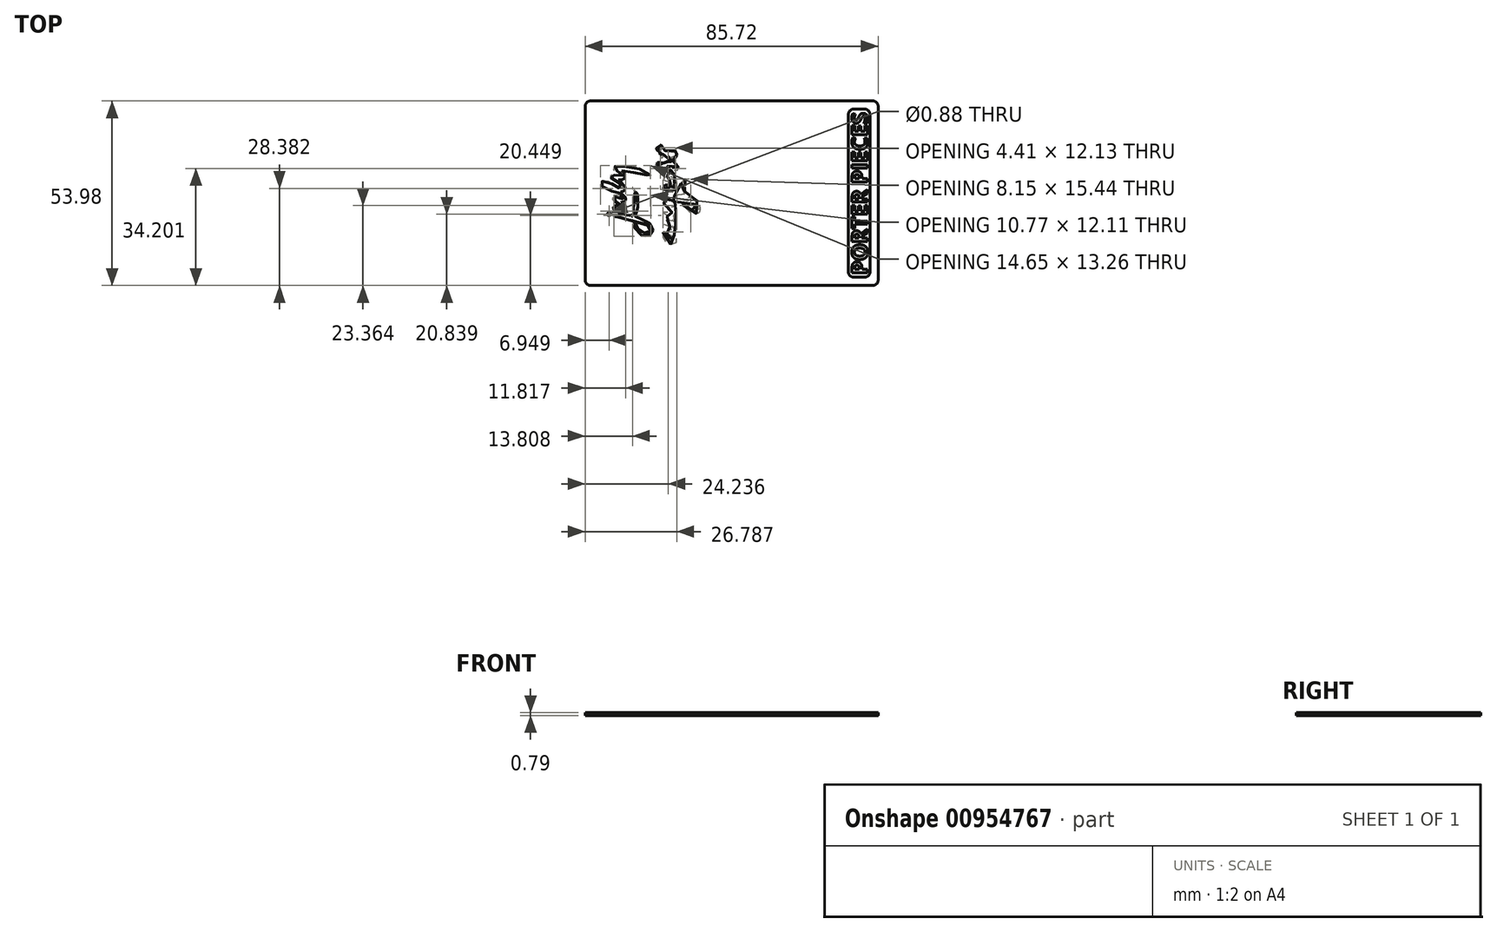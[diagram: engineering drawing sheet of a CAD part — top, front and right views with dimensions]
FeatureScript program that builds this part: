
annotation { "Feature Type Name" : "Feature", "Feature Type Description" : "" }
export const myFeature = defineFeature(function(context is Context, id is Id, definition is map)
    precondition{}
    {
        {
            var Q0;
            Q0=qCreatedBy(makeId("Top.planeOp"),FACE);
            var sketch = newSketch(context, id + "F0", { "sketchPlane" : qUnion([Q0])});
            skLineSegment(sketch, "E0.bottom", {"start": v(42.86, 26.99) * mm, "end": v(-42.86, 26.99) * mm});
            skLineSegment(sketch, "E0.top", {"start": v(42.86, -26.99) * mm, "end": v(-42.86, -26.99) * mm});
            skLineSegment(sketch, "E0.left", {"start": v(42.86, 26.99) * mm, "end": v(42.86, -26.99) * mm});
            skLineSegment(sketch, "E0.right", {"start": v(-42.86, 26.99) * mm, "end": v(-42.86, -26.99) * mm});
            skPoint(sketch, "E0.middle", {"position": v(0, 0) * mm});
            skSolve(sketch);
        }
        {
            var Q0;
            Q0=makeQuery(id+"F0.imprint","IMPRINT",FACE,{"disambiguationData":[TD([[makeQuery(id+"F0.imprint","IMPRINT",EDGE,{"derivedFrom":sQuery(id+"F0.wireOp",EDGE,"E0.bottom")}),1.0]])]});
            extrude(context, id + "F1", {"entities" : qUnion([Q0]), "depth" : 0.8 * mm, "offsetDistance" : 25.4 * mm});
        }
        {
            var Q0;
            Q0=makeQuery(id+"F1.opExtrude","SWEPT_EDGE",EDGE,{"disambiguationData":[OSD([sQuery(id+"F0.wireOp",EDGE,"E0.bottom"),sQuery(id+"F0.wireOp",EDGE,"E0.left")])]});
            var Q1;
            Q1=makeQuery(id+"F1.opExtrude","SWEPT_EDGE",EDGE,{"disambiguationData":[OSD([sQuery(id+"F0.wireOp",EDGE,"E0.bottom"),sQuery(id+"F0.wireOp",EDGE,"E0.right")])]});
            var Q2;
            Q2=makeQuery(id+"F1.opExtrude","SWEPT_EDGE",EDGE,{"disambiguationData":[OSD([sQuery(id+"F0.wireOp",EDGE,"E0.top"),sQuery(id+"F0.wireOp",EDGE,"E0.right")])]});
            var Q3;
            Q3=makeQuery(id+"F1.opExtrude","SWEPT_EDGE",EDGE,{"disambiguationData":[OSD([sQuery(id+"F0.wireOp",EDGE,"E0.top"),sQuery(id+"F0.wireOp",EDGE,"E0.left")])]});
            fillet(context, id + "F2", {"entities" : qUnion([Q0, Q1, Q2, Q3]), "radius" : 1.59 * mm, "tangentPropagation" : true, "allowEdgeOverflow" : false});
        }
        {
            var Q0;
            Q0=makeQuery(id+"F1.opExtrude","CAP_FACE",FACE,{"disambiguationData":[OSD([sQuery(id+"F0.wireOp",EDGE,"E0.bottom"),sQuery(id+"F0.wireOp",EDGE,"E0.top"),sQuery(id+"F0.wireOp",EDGE,"E0.left"),sQuery(id+"F0.wireOp",EDGE,"E0.right")])],"isStart":false});
            var sketch = newSketch(context, id + "F3", { "sketchPlane" : qUnion([Q0])});
            skLineSegment(sketch, "E1.bottom", {"start": v(34.13, -24.6) * mm, "end": v(40.48, -24.6) * mm});
            skLineSegment(sketch, "E1.top", {"start": v(34.13, 24.6) * mm, "end": v(40.48, 24.6) * mm});
            skLineSegment(sketch, "E1.left", {"start": v(34.13, -24.6) * mm, "end": v(34.13, 24.6) * mm});
            skLineSegment(sketch, "E1.right", {"start": v(40.48, -24.6) * mm, "end": v(40.48, 24.6) * mm});
            skSolve(sketch);
        }
        {
            var Q0;
            Q0=makeQuery(id+"F3.imprint","IMPRINT",FACE,{"disambiguationData":[TD([[makeQuery(id+"F3.imprint","IMPRINT",EDGE,{"derivedFrom":sQuery(id+"F3.wireOp",EDGE,"E1.bottom")}),1.0]])]});
            extrude(context, id + "F4", {"entities" : qUnion([Q0]), "operationType" : NewBodyOperationType.REMOVE, "oppositeDirection" : true, "depth" : 0.4 * mm, "offsetDistance" : 25.4 * mm});
        }
        {
            var Q0;
            Q0=makeQuery(id+"F4.boolean.opBoolean","COPY",EDGE,{"derivedFrom":makeQuery(id+"F4.opExtrude","SWEPT_EDGE",EDGE,{"disambiguationData":[OSD([sQuery(id+"F3.wireOp",EDGE,"E1.bottom"),sQuery(id+"F3.wireOp",EDGE,"E1.left")])]})});
            var Q1;
            Q1=makeQuery(id+"F4.boolean.opBoolean","COPY",EDGE,{"derivedFrom":makeQuery(id+"F4.opExtrude","SWEPT_EDGE",EDGE,{"disambiguationData":[OSD([sQuery(id+"F3.wireOp",EDGE,"E1.bottom"),sQuery(id+"F3.wireOp",EDGE,"E1.right")])]})});
            var Q2;
            Q2=makeQuery(id+"F4.boolean.opBoolean","COPY",EDGE,{"derivedFrom":makeQuery(id+"F4.opExtrude","SWEPT_EDGE",EDGE,{"disambiguationData":[OSD([sQuery(id+"F3.wireOp",EDGE,"E1.top"),sQuery(id+"F3.wireOp",EDGE,"E1.right")])]})});
            var Q3;
            Q3=makeQuery(id+"F4.boolean.opBoolean","COPY",EDGE,{"derivedFrom":makeQuery(id+"F4.opExtrude","SWEPT_EDGE",EDGE,{"disambiguationData":[OSD([sQuery(id+"F3.wireOp",EDGE,"E1.top"),sQuery(id+"F3.wireOp",EDGE,"E1.left")])]})});
            fillet(context, id + "F5", {"entities" : qUnion([Q0, Q1, Q2, Q3]), "radius" : 1.59 * mm, "tangentPropagation" : true, "allowEdgeOverflow" : false});
        }
        {
            var Q0;
            Q0=makeQuery(id+"F4.boolean.opBoolean","COPY",FACE,{"derivedFrom":makeQuery(id+"F4.opExtrude","CAP_FACE",FACE,{"disambiguationData":[OSD([sQuery(id+"F3.wireOp",EDGE,"E1.bottom"),sQuery(id+"F3.wireOp",EDGE,"E1.top"),sQuery(id+"F3.wireOp",EDGE,"E1.left"),sQuery(id+"F3.wireOp",EDGE,"E1.right")])],"isStart":false})});
            var sketch = newSketch(context, id + "F6", { "sketchPlane" : qUnion([Q0])});
            skText(sketch, "E2", { "text": "PORTER PIECES", "fontName": "OpenSans-Bold.ttf"});
            const initialGuessF6  = {"E2": [0.03976, -0.02381, 0, 1, 0.00461]};
            skSetInitialGuess(sketch, initialGuessF6);
            skSolve(sketch);
        }
        {
            var Q0;
            Q0=makeQuery(id+"F6.imprint","IMPRINT",FACE,{"disambiguationData":[TD([[makeQuery(id+"F6.imprint","IMPRINT",EDGE,{"derivedFrom":sQuery(id+"F6.wireOp",EDGE,"E2.sketch_text.stroke-0")}),-1.0]])]});
            var Q1;
            Q1=makeQuery(id+"F6.imprint","IMPRINT",FACE,{"disambiguationData":[TD([[makeQuery(id+"F6.imprint","IMPRINT",EDGE,{"derivedFrom":sQuery(id+"F6.wireOp",EDGE,"E2.sketch_text.stroke-16")}),-1.0]])]});
            var Q2;
            Q2=makeQuery(id+"F6.imprint","IMPRINT",FACE,{"disambiguationData":[TD([[makeQuery(id+"F6.imprint","IMPRINT",EDGE,{"derivedFrom":sQuery(id+"F6.wireOp",EDGE,"E2.sketch_text.stroke-30")}),-1.0]])]});
            var Q3;
            Q3=makeQuery(id+"F6.imprint","IMPRINT",FACE,{"disambiguationData":[TD([[makeQuery(id+"F6.imprint","IMPRINT",EDGE,{"derivedFrom":sQuery(id+"F6.wireOp",EDGE,"E2.sketch_text.stroke-49")}),-1.0]])]});
            var Q4;
            Q4=makeQuery(id+"F6.imprint","IMPRINT",FACE,{"disambiguationData":[TD([[makeQuery(id+"F6.imprint","IMPRINT",EDGE,{"derivedFrom":sQuery(id+"F6.wireOp",EDGE,"E2.sketch_text.stroke-57")}),-1.0]])]});
            var Q5;
            Q5=makeQuery(id+"F6.imprint","IMPRINT",FACE,{"disambiguationData":[TD([[makeQuery(id+"F6.imprint","IMPRINT",EDGE,{"derivedFrom":sQuery(id+"F6.wireOp",EDGE,"E2.sketch_text.stroke-69")}),-1.0]])]});
            var Q6;
            Q6=makeQuery(id+"F6.imprint","IMPRINT",FACE,{"disambiguationData":[TD([[makeQuery(id+"F6.imprint","IMPRINT",EDGE,{"derivedFrom":sQuery(id+"F6.wireOp",EDGE,"E2.sketch_text.stroke-88")}),-1.0]])]});
            var Q7;
            Q7=makeQuery(id+"F6.imprint","IMPRINT",FACE,{"disambiguationData":[TD([[makeQuery(id+"F6.imprint","IMPRINT",EDGE,{"derivedFrom":sQuery(id+"F6.wireOp",EDGE,"E2.sketch_text.stroke-104")}),-1.0]])]});
            var Q8;
            Q8=makeQuery(id+"F6.imprint","IMPRINT",FACE,{"disambiguationData":[TD([[makeQuery(id+"F6.imprint","IMPRINT",EDGE,{"derivedFrom":sQuery(id+"F6.wireOp",EDGE,"E2.sketch_text.stroke-108")}),-1.0]])]});
            var Q9;
            Q9=makeQuery(id+"F6.imprint","IMPRINT",FACE,{"disambiguationData":[TD([[makeQuery(id+"F6.imprint","IMPRINT",EDGE,{"derivedFrom":sQuery(id+"F6.wireOp",EDGE,"E2.sketch_text.stroke-120")}),-1.0]])]});
            var Q10;
            Q10=makeQuery(id+"F6.imprint","IMPRINT",FACE,{"disambiguationData":[TD([[makeQuery(id+"F6.imprint","IMPRINT",EDGE,{"derivedFrom":sQuery(id+"F6.wireOp",EDGE,"E2.sketch_text.stroke-135")}),-1.0]])]});
            var Q11;
            Q11=makeQuery(id+"F6.imprint","IMPRINT",FACE,{"disambiguationData":[TD([[makeQuery(id+"F6.imprint","IMPRINT",EDGE,{"derivedFrom":sQuery(id+"F6.wireOp",EDGE,"E2.sketch_text.stroke-147")}),-1.0]])]});
            extrude(context, id + "F7", {"entities" : qUnion([Q0, Q1, Q2, Q3, Q4, Q5, Q6, Q7, Q8, Q9, Q10, Q11]), "operationType" : NewBodyOperationType.ADD, "depth" : 0.4 * mm, "offsetDistance" : 25.4 * mm});
        }
        {
            var Q0;
            Q0=makeQuery(id+"F1.opExtrude","CAP_FACE",FACE,{"disambiguationData":[OSD([sQuery(id+"F0.wireOp",EDGE,"E0.bottom"),sQuery(id+"F0.wireOp",EDGE,"E0.top"),sQuery(id+"F0.wireOp",EDGE,"E0.left"),sQuery(id+"F0.wireOp",EDGE,"E0.right")])],"isStart":false});
            var sketch = newSketch(context, id + "F8", { "sketchPlane" : qUnion([Q0])});
            skCircle(sketch, "E3", {"center": v(-35.91, -6.15) * mm, "radius": 0.44 * mm});
            skFitSpline(sketch, "E4", {"points": [v(-34.44, -6.56) * mm, v(-25.28, -9.09) * mm, v(-23.7, -10.25) * mm, v(-23.86, -11.28) * mm, v(-25.2, -11.61) * mm, v(-26.7, -11.05) * mm, v(-27.78, -9.76) * mm, v(-28.14, -8.54) * mm, v(-28.63, -8.54) * mm, v(-27.89, -10.97) * mm, v(-25.93, -12.44) * mm, v(-24.2, -12.49) * mm, v(-23.2, -11.61) * mm, v(-23.09, -10.01) * mm, v(-24.04, -8.72) * mm, v(-25.51, -7.95) * mm, v(-28.17, -6.97) * mm, v(-28.22, -6.74) * mm, v(-27.58, -4.4) * mm, v(-27.4, -1.94) * mm, v(-27.47, -1.53) * mm, v(-27.73, 0) * mm, v(-28.53, 0.82) * mm, v(-28.32, 0) * mm, v(-28.27, -1.53) * mm, v(-28.5, -3.26) * mm, v(-28.79, -4.16) * mm, v(-28.79, -5.78) * mm, v(-28.79, -6.76) * mm, v(-29.33, -6.69) * mm, v(-31.6, -6.12) * mm, v(-33.53, -6.25) * mm, v(-34.44, -6.56) * mm]});
            skFitSpline(sketch, "E5", {"points": [v(-34.71, -4.48) * mm, v(-33.91, -4.94) * mm, v(-32.35, -5.25) * mm, v(-31.24, -4.97) * mm, v(-31.03, -3.8) * mm, v(-32.38, -2.67) * mm], "startDerivative": vector(4.17, -2.95) * mm, "endDerivative": vector(-7.48, 4.2) * mm});
            skFitSpline(sketch, "E6", {"points": [v(-32.38, -2.67) * mm, v(-31.3, -2.36) * mm, v(-31.06, -1.35) * mm, v(-32.38, 0) * mm, v(-32.38, 0.3) * mm, v(-31.8, 0.55) * mm, v(-31.12, 1.5) * mm, v(-31.8, 2.57) * mm, v(-33.18, 3.92) * mm], "startDerivative": vector(9.47, 0.91) * mm, "endDerivative": vector(-8.51, 8.28) * mm});
            skFitSpline(sketch, "E7", {"points": [v(-33.18, 3.92) * mm, v(-32.38, 3.92) * mm, v(-31.37, 4.41) * mm, v(-31.34, 5.64) * mm, v(-32.13, 6.62) * mm], "startDerivative": vector(3.47, -0.29) * mm, "endDerivative": vector(-3.5, 3.23) * mm});
            skFitSpline(sketch, "E8", {"points": [v(-32.13, 6.62) * mm, v(-29.99, 6.33) * mm, v(-26.77, 5.67) * mm, v(-25.3, 5.4) * mm, v(-23.85, 4.72) * mm, v(-23.8, 5.21) * mm, v(-26.25, 6.62) * mm, v(-28, 7.51) * mm, v(-32.13, 7.82) * mm, v(-33.94, 7.94) * mm, v(-34.74, 7.05) * mm, v(-33.82, 6.62) * mm, v(-32.86, 6.33) * mm, v(-31.82, 5.33) * mm, v(-32.58, 5.09) * mm, v(-34.14, 5.26) * mm, v(-34.75, 5.41) * mm, v(-35.48, 4.9) * mm, v(-35.24, 4.44) * mm, v(-33.84, 3.72) * mm, v(-31.82, 1.8) * mm, v(-31.82, 1.53) * mm, v(-33.7, 1.66) * mm, v(-34.36, 2.07) * mm, v(-36.05, 3.35) * mm, v(-37.74, 3.5) * mm, v(-38.28, 3.35) * mm, v(-38.35, 2.66) * mm, v(-37.44, 1.68) * mm, v(-35.53, 0.75) * mm, v(-34.14, 0.4) * mm, v(-33.2, 0.27) * mm, v(-32.77, -0.28) * mm, v(-31.82, -1.44) * mm, v(-31.82, -1.64) * mm, v(-33.05, -1.35) * mm, v(-34.07, -1) * mm, v(-35.07, -1.77) * mm, v(-34, -2.44) * mm, v(-32.92, -2.83) * mm, v(-31.82, -3.96) * mm, v(-31.82, -4.17) * mm, v(-33.16, -3.72) * mm, v(-34.14, -3.7) * mm, v(-34.94, -4.26) * mm, v(-34.71, -4.48) * mm], "startDerivative": vector(66.7, -6.48) * mm, "endDerivative": vector(32.5, -16.52) * mm});
            skFitSpline(sketch, "E9", {"points": [v(-20.07, -12.49) * mm, v(-19.93, -14.3) * mm, v(-18.5, -15.78) * mm, v(-16.37, -15.78) * mm, v(-15.95, -14.2) * mm, v(-16.74, -13.47) * mm, v(-16.09, -12.49) * mm, v(-17.38, -10.87) * mm, v(-16.04, -9.8) * mm, v(-17.2, -7.95) * mm, v(-16.09, -7.21) * mm, v(-17.38, -5.13) * mm, v(-16.04, -4.62) * mm, v(-16.83, -3) * mm, v(-10.67, -4.1) * mm, v(-9.74, -5.54) * mm, v(-9.97, -6.33) * mm, v(-11.32, -6.29) * mm, v(-12.84, -4.9) * mm, v(-13.35, -4.06) * mm, v(-14.05, -4.3) * mm, v(-13.08, -5.78) * mm, v(-11.6, -6.84) * mm, v(-9.79, -6.93) * mm, v(-9.1, -6.05) * mm, v(-9.74, -3.83) * mm, v(-12.15, -2.49) * mm, v(-13.68, -2.07) * mm, v(-13.59, 2.6) * mm, v(-14.23, 3.12) * mm, v(-14.6, 0.48) * mm, v(-14.65, -1.98) * mm, v(-17.8, -1.7) * mm, v(-18.87, -2.35) * mm, v(-17.48, -2.95) * mm, v(-16.64, -4.06) * mm, v(-17.62, -4.06) * mm, v(-19.2, -2.95) * mm, v(-19.84, -1.88) * mm, v(-20.26, -1.93) * mm, v(-19.98, -3.83) * mm, v(-18.87, -5.08) * mm, v(-18.17, -5.4) * mm, v(-17.25, -6.7) * mm, v(-19.56, -6.47) * mm, v(-19.98, -7.35) * mm, v(-17.94, -8.14) * mm, v(-16.88, -9.34) * mm, v(-17.76, -9.3) * mm, v(-19.6, -9.11) * mm, v(-20.03, -10.27) * mm, v(-18.03, -10.92) * mm, v(-17.2, -12.12) * mm, v(-18.31, -12.08) * mm, v(-18.96, -13) * mm, v(-17.48, -13.51) * mm, v(-16.55, -14.58) * mm, v(-17.57, -14.44) * mm, v(-19.47, -13.37) * mm, v(-19.38, -12.49) * mm, v(-20.07, -12.49) * mm]});
            skFitSpline(sketch, "E10", {"points": [v(-19.84, 0) * mm, v(-17.38, -0.8) * mm, v(-16.04, 0) * mm, v(-16.04, 1.02) * mm, v(-16.7, 2.17) * mm, v(-16.04, 2.36) * mm, v(-16.04, 3) * mm, v(-17.2, 4.95) * mm, v(-19.02, 6.62) * mm, v(-17.38, 6.9) * mm, v(-16.52, 7.03) * mm, v(-16.04, 6.45) * mm, v(-16.3, 6.1) * mm, v(-16.83, 6.76) * mm, v(-17.2, 6.43) * mm, v(-16.55, 5.6) * mm, v(-15.67, 5.77) * mm, v(-15.8, 7.34) * mm, v(-16.58, 8.02) * mm, v(-17, 8.02) * mm, v(-17.38, 9.43) * mm, v(-16.74, 9.68) * mm, v(-15.7, 10.53) * mm, v(-16.04, 11.63) * mm, v(-16.47, 11.58) * mm, v(-16.38, 10.97) * mm, v(-17.73, 10.94) * mm, v(-19.84, 11.52) * mm, v(-19.84, 12.07) * mm, v(-20.46, 12.96) * mm, v(-20.9, 12.7) * mm, v(-20.57, 11.72) * mm, v(-21.54, 12.24) * mm, v(-21.9, 11.63) * mm, v(-20.76, 10.75) * mm, v(-20.8, 9.48) * mm, v(-20.1, 9.37) * mm, v(-20.19, 10.34) * mm, v(-19.84, 10.17) * mm, v(-18.45, 9.62) * mm, v(-17.79, 8.02) * mm, v(-18.23, 8.1) * mm, v(-20.16, 7.64) * mm, v(-21.12, 7.89) * mm, v(-21.87, 7.4) * mm, v(-21.32, 6.62) * mm, v(-19.84, 6.48) * mm, v(-16.77, 3.4) * mm, v(-18.97, 3.84) * mm, v(-19.84, 2.85) * mm, v(-17.38, 2.02) * mm, v(-16.58, 0.86) * mm, v(-18.23, 0.97) * mm, v(-19.41, 1.2) * mm, v(-19.84, 0) * mm]});
            skSolve(sketch);
        }
        {
            var Q0;
            Q0=makeQuery(id+"F8.imprint","IMPRINT",FACE,{"disambiguationData":[TD([[makeQuery(id+"F8.imprint","IMPRINT",EDGE,{"derivedFrom":sQuery(id+"F8.wireOp",EDGE,"E5")}),1.0]])]});
            var Q1;
            Q1=makeQuery(id+"F8.imprint","IMPRINT",FACE,{"disambiguationData":[TD([[makeQuery(id+"F8.imprint","IMPRINT",EDGE,{"derivedFrom":sQuery(id+"F8.wireOp",EDGE,"E4")}),1.0]])]});
            var Q2;
            Q2=makeQuery(id+"F8.imprint","IMPRINT",FACE,{"disambiguationData":[TD([[makeQuery(id+"F8.imprint","IMPRINT",EDGE,{"derivedFrom":sQuery(id+"F8.wireOp",EDGE,"E3")}),1.0]])]});
            extrude(context, id + "F9", {"entities" : qUnion([Q0, Q1, Q2]), "operationType" : NewBodyOperationType.REMOVE, "oppositeDirection" : true, "depth" : 25.4 * mm, "offsetDistance" : 25.4 * mm});
        }
        {
            var Q0;
            Q0=makeQuery(id+"F1.opExtrude","CAP_FACE",FACE,{"disambiguationData":[OSD([sQuery(id+"F0.wireOp",EDGE,"E0.bottom"),sQuery(id+"F0.wireOp",EDGE,"E0.top"),sQuery(id+"F0.wireOp",EDGE,"E0.left"),sQuery(id+"F0.wireOp",EDGE,"E0.right")])],"isStart":false});
            var sketch = newSketch(context, id + "F10", { "sketchPlane" : qUnion([Q0])});
            skFitSpline(sketch, "E11", {"points": [v(-20.15, -11.34) * mm, v(-20, -13.15) * mm, v(-18.57, -14.64) * mm, v(-16.44, -14.64) * mm, v(-16.02, -13.06) * mm, v(-16.81, -12.32) * mm, v(-16.16, -11.34) * mm, v(-17.46, -9.73) * mm, v(-16.12, -8.66) * mm, v(-17.27, -6.8) * mm, v(-16.16, -6.07) * mm, v(-17.46, -3.98) * mm, v(-16.12, -3.47) * mm, v(-16.9, -1.85) * mm, v(-10.74, -2.96) * mm, v(-9.81, -4.4) * mm, v(-10.05, -5.19) * mm, v(-11.39, -5.14) * mm, v(-12.92, -3.75) * mm, v(-13.43, -2.92) * mm, v(-14.12, -3.15) * mm, v(-13.15, -4.63) * mm, v(-11.67, -5.7) * mm, v(-9.86, -5.79) * mm, v(-9.17, -4.9) * mm, v(-9.81, -2.68) * mm, v(-12.22, -1.34) * mm, v(-13.75, -0.92) * mm, v(-13.66, 3.76) * mm, v(-14.3, 4.26) * mm, v(-14.68, 1.62) * mm, v(-14.73, -0.83) * mm, v(-17.88, -0.55) * mm, v(-18.94, -1.2) * mm, v(-17.55, -1.8) * mm, v(-16.72, -2.92) * mm, v(-17.7, -2.92) * mm, v(-19.27, -1.8) * mm, v(-19.91, -0.74) * mm, v(-20.33, -0.78) * mm, v(-20.05, -2.68) * mm, v(-18.94, -3.94) * mm, v(-18.25, -4.26) * mm, v(-17.32, -5.56) * mm, v(-19.64, -5.33) * mm, v(-20.05, -6.2) * mm, v(-18.01, -7) * mm, v(-16.95, -8.2) * mm, v(-17.83, -8.15) * mm, v(-19.68, -7.97) * mm, v(-20.1, -9.12) * mm, v(-18.1, -9.77) * mm, v(-17.27, -10.98) * mm, v(-18.39, -10.93) * mm, v(-19.03, -11.86) * mm, v(-17.55, -12.37) * mm, v(-16.62, -13.43) * mm, v(-17.64, -13.3) * mm, v(-19.54, -12.23) * mm, v(-19.45, -11.34) * mm, v(-20.15, -11.34) * mm]});
            skFitSpline(sketch, "E12", {"points": [v(-19.91, 1.15) * mm, v(-17.46, 0.35) * mm, v(-16.12, 1.15) * mm, v(-16.12, 2.16) * mm, v(-16.78, 3.32) * mm, v(-16.12, 3.5) * mm, v(-16.12, 4.15) * mm, v(-17.27, 6.1) * mm, v(-19.1, 7.77) * mm, v(-17.46, 8.04) * mm, v(-16.6, 8.18) * mm, v(-16.12, 7.6) * mm, v(-16.38, 7.24) * mm, v(-16.9, 7.9) * mm, v(-17.27, 7.57) * mm, v(-16.62, 6.75) * mm, v(-15.74, 6.91) * mm, v(-15.88, 8.48) * mm, v(-16.65, 9.17) * mm, v(-17.06, 9.17) * mm, v(-17.46, 10.58) * mm, v(-16.82, 10.82) * mm, v(-15.77, 11.68) * mm, v(-16.12, 12.78) * mm, v(-16.54, 12.72) * mm, v(-16.46, 12.12) * mm, v(-17.8, 12.1) * mm, v(-19.91, 12.67) * mm, v(-19.91, 13.22) * mm, v(-20.54, 14.1) * mm, v(-20.98, 13.85) * mm, v(-20.65, 12.86) * mm, v(-21.6, 13.39) * mm, v(-21.97, 12.78) * mm, v(-20.84, 11.9) * mm, v(-20.87, 10.63) * mm, v(-20.18, 10.52) * mm, v(-20.26, 11.48) * mm, v(-19.91, 11.32) * mm, v(-18.52, 10.77) * mm, v(-17.86, 9.17) * mm, v(-18.3, 9.25) * mm, v(-20.23, 8.78) * mm, v(-21.2, 9.03) * mm, v(-21.94, 8.54) * mm, v(-21.39, 7.77) * mm, v(-19.91, 7.63) * mm, v(-16.84, 4.54) * mm, v(-19.05, 4.98) * mm, v(-19.91, 4) * mm, v(-17.46, 3.17) * mm, v(-16.65, 2) * mm, v(-18.3, 2.12) * mm, v(-19.49, 2.34) * mm, v(-19.91, 1.15) * mm]});
            skSolve(sketch);
        }
        {
            var Q0;
            Q0 = qSketchRegion(id + "F10", true);
            extrude(context, id + "F11", {"entities" : qUnion([Q0]), "operationType" : NewBodyOperationType.REMOVE, "oppositeDirection" : true, "depth" : 25.4 * mm, "offsetDistance" : 25.4 * mm});
        }
    });
